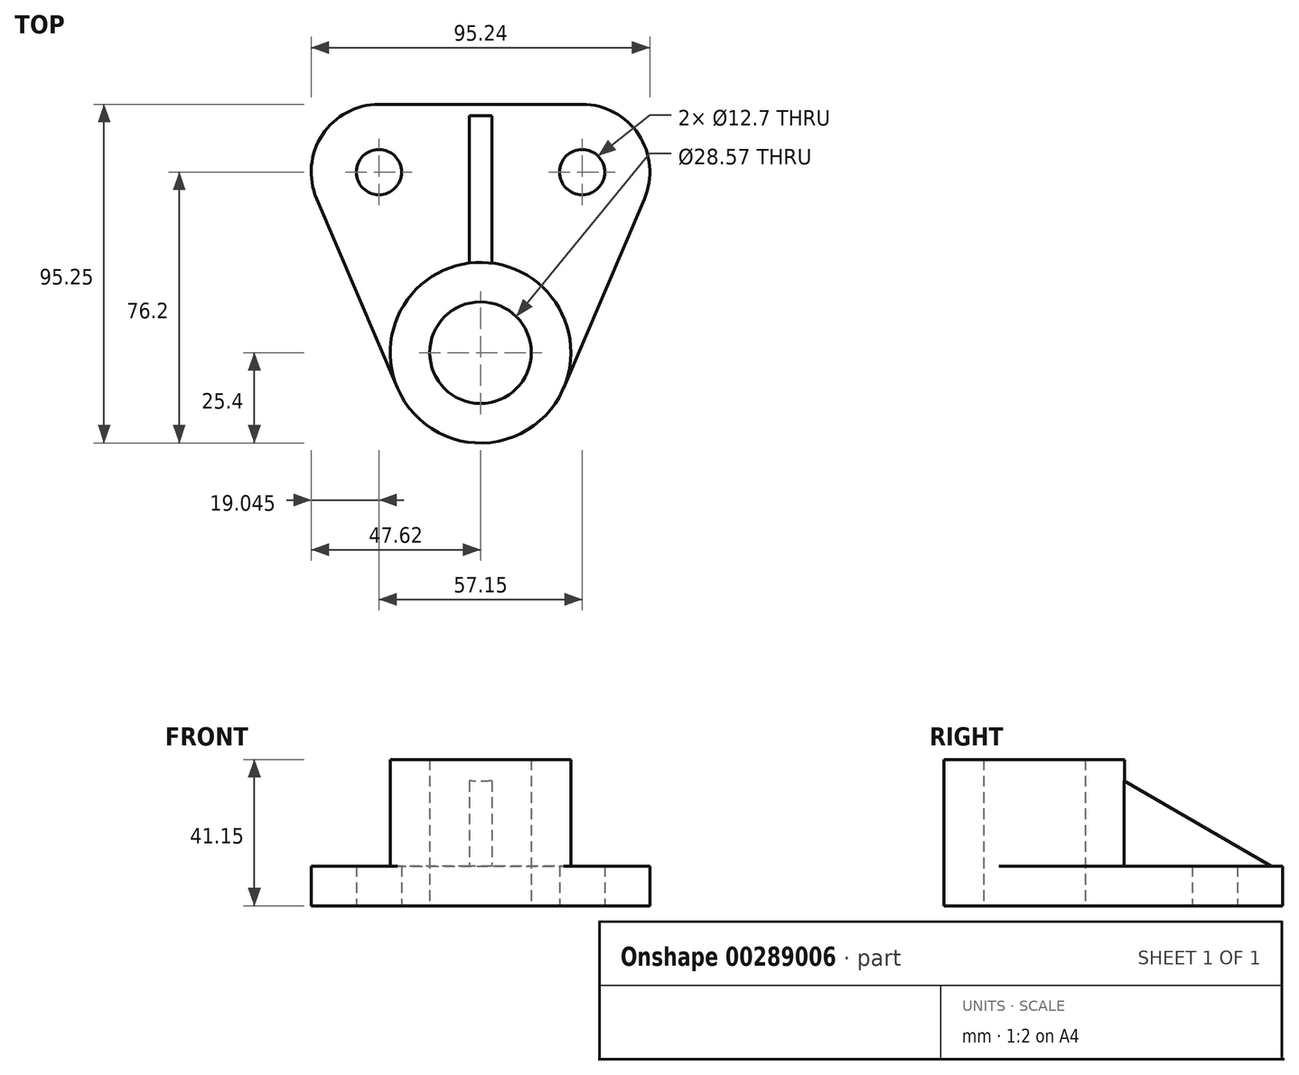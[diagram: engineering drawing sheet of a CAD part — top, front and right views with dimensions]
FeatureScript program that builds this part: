
annotation { "Feature Type Name" : "Feature", "Feature Type Description" : "" }
export const myFeature = defineFeature(function(context is Context, id is Id, definition is map)
    precondition{}
    {
        {
            var Q0;
            Q0=qCreatedBy(makeId("Top.planeOp"),FACE);
            var sketch = newSketch(context, id + "F0", { "sketchPlane" : qUnion([Q0])});
            skCircle(sketch, "E0", {"center": v(0, 0) * mm, "radius": 25.4 * mm});
            skLineSegment(sketch, "E1", {"start": v(0, 0) * mm, "end": v(0, 69.85) * mm, "construction": true});
            skLineSegment(sketch, "E2", {"start": v(-23.36, -9.97) * mm, "end": v(-46.1, 43.33) * mm});
            skArc(sketch, "E3.filletArc", {"start": v(-28.58, 69.85) * mm, "mid": v(-44.47, 61.3) * mm, "end": v(-46.1, 43.33) * mm});
            skCircle(sketch, "E4", {"center": v(0, 0) * mm, "radius": 14.29 * mm});
            skCircle(sketch, "E5", {"center": v(-28.58, 50.8) * mm, "radius": 6.35 * mm});
            skArc(sketch, "E6.0.MirrorCS", {"start": v(28.58, 69.85) * mm, "mid": v(44.47, 61.3) * mm, "end": v(46.1, 43.33) * mm});
            skLineSegment(sketch, "E7.0.MirrorCS", {"start": v(23.36, -9.97) * mm, "end": v(46.1, 43.33) * mm});
            skCircle(sketch, "E8.0.MirrorC", {"center": v(28.58, 50.8) * mm, "radius": 6.35 * mm});
            skLineSegment(sketch, "E9", {"start": v(-28.58, 69.85) * mm, "end": v(28.58, 69.85) * mm});
            skSolve(sketch);
        }
        {
            var Q0;
            Q0=makeQuery(id+"F0.imprint","IMPRINT",FACE,{"disambiguationData":[TD([[makeQuery(id+"F0.imprint","IMPRINT",EDGE,{"derivedFrom":sQuery(id+"F0.wireOp",EDGE,"E4")}),-1.0]])]});
            extrude(context, id + "F1", {"entities" : qUnion([Q0]), "depth" : 41.15 * mm});
        }
        {
            var Q0;
            {var subQ1=sQuery(id+"F0.wireOp",EDGE,"E2");Q0=makeQuery(id+"F0.imprint","IMPRINT",FACE,{"disambiguationData":[TD([[makeQuery(id+"F0.imprint","IMPRINT",EDGE,{"derivedFrom":subQ1}),-1.0]])]});}
            extrude(context, id + "F2", {"entities" : qUnion([Q0]), "operationType" : NewBodyOperationType.ADD, "depth" : 11.18 * mm});
        }
        {
            var Q0;
            Q0=qCreatedBy(makeId("Right.planeOp"),FACE);
            var sketch = newSketch(context, id + "F3", { "sketchPlane" : qUnion([Q0])});
            skLineSegment(sketch, "E10", {"start": v(-25.4, 0) * mm, "end": v(-25.4, 41.15) * mm});
            skLineSegment(sketch, "E11", {"start": v(25.4, 41.97) * mm, "end": v(25.4, 11.18) * mm});
            skLineSegment(sketch, "E12.0", {"start": v(22.23, 41.97) * mm, "end": v(22.23, 11.18) * mm});
            skLineSegment(sketch, "E13", {"start": v(22.23, 36.84) * mm, "end": v(66.67, 11.18) * mm});
            skLineSegment(sketch, "E14", {"start": v(66.67, 11.18) * mm, "end": v(22.23, 11.18) * mm});
            skLineSegment(sketch, "E15", {"start": v(22.22, 11.18) * mm, "end": v(22.23, 36.84) * mm});
            skSolve(sketch);
        }
        {
            var Q0;
            Q0=qSketchRegion(id+"F3",true);
            extrude(context, id + "F4", {"entities" : qUnion([Q0]), "operationType" : NewBodyOperationType.ADD, "endBound" : BoundingType.SYMMETRIC, "depth" : 6.35 * mm});
        }
    });
